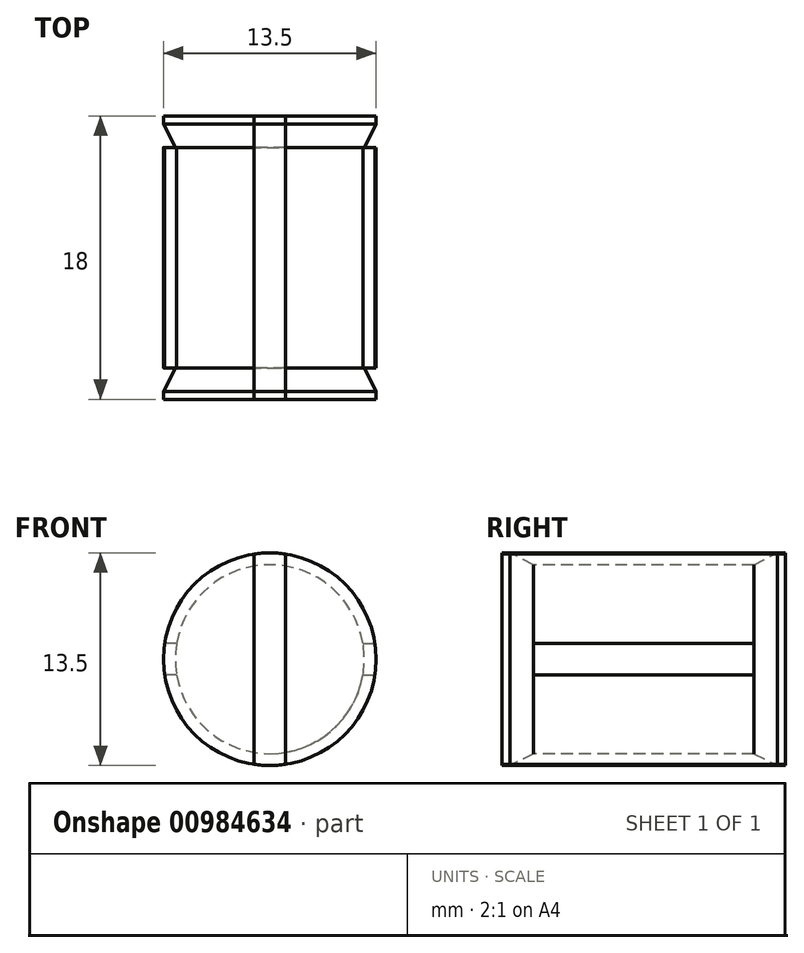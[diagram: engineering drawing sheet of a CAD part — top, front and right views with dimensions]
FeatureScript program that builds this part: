
annotation { "Feature Type Name" : "Feature", "Feature Type Description" : "" }
export const myFeature = defineFeature(function(context is Context, id is Id, definition is map)
    precondition{}
    {
        {
            var Q0;
            Q0=qCreatedBy(makeId("Top.planeOp"),FACE);
            var sketch = newSketch(context, id + "F0", { "sketchPlane" : qUnion([Q0])});
            skLineSegment(sketch, "E0", {"start": v(0, 0) * mm, "end": v(0, 11.4) * mm, "construction": true});
            skLineSegment(sketch, "E1.bottom", {"start": v(0, 19.36) * mm, "end": v(-6, 19.36) * mm});
            skLineSegment(sketch, "E1.top", {"start": v(0, 1.36) * mm, "end": v(-6, 1.36) * mm});
            skLineSegment(sketch, "E1.left", {"start": v(0, 19.36) * mm, "end": v(0, 1.36) * mm});
            skLineSegment(sketch, "E1.right", {"start": v(-6, 19.36) * mm, "end": v(-6, 1.36) * mm});
            skLineSegment(sketch, "E2.bottom", {"start": v(-6, 17.36) * mm, "end": v(-21, 17.36) * mm});
            skLineSegment(sketch, "E2.top", {"start": v(-6, 3.36) * mm, "end": v(-21, 3.36) * mm});
            skLineSegment(sketch, "E2.left", {"start": v(-6, 17.36) * mm, "end": v(-6, 3.36) * mm});
            skLineSegment(sketch, "E2.right", {"start": v(-21, 17.36) * mm, "end": v(-21, 3.36) * mm});
            skLineSegment(sketch, "E3", {"start": v(-3.75, 17.36) * mm, "end": v(-3.75, 19.36) * mm, "construction": true});
            skLineSegment(sketch, "E4", {"start": v(-3.85, 3.36) * mm, "end": v(-3.85, 1.36) * mm, "construction": true});
            skLineSegment(sketch, "E5", {"start": v(-15, 17.36) * mm, "end": v(-15, 3.36) * mm});
            skPoint(sketch, "E6", {"position": v(-18, 10.36) * mm});
            skPoint(sketch, "E6.positionSnap0", {"position": v(-21, 10.36) * mm});
            skLineSegment(sketch, "E7", {"start": v(-18, 10.36) * mm, "end": v(-21, 10.36) * mm, "construction": true});
            skCircle(sketch, "E8", {"center": v(-18, 10.36) * mm, "radius": 1.6 * mm});
            skLineSegment(sketch, "E9", {"start": v(-6.75, 19.36) * mm, "end": v(-6, 19.36) * mm});
            skLineSegment(sketch, "E10", {"start": v(-6.75, 19.36) * mm, "end": v(-6.75, 18.86) * mm});
            skLineSegment(sketch, "E11", {"start": v(-6.75, 18.86) * mm, "end": v(-6, 17.36) * mm});
            skLineSegment(sketch, "E12", {"start": v(0, 10.36) * mm, "end": v(-8.05, 10.36) * mm, "construction": true});
            skLineSegment(sketch, "E13.MirrorCS", {"start": v(-6.75, 1.86) * mm, "end": v(-6, 3.36) * mm});
            skLineSegment(sketch, "E14.MirrorCS", {"start": v(-6.75, 1.36) * mm, "end": v(-6, 1.36) * mm});
            skLineSegment(sketch, "E15.MirrorCS", {"start": v(-6.75, 1.36) * mm, "end": v(-6.75, 1.86) * mm});
            skSolve(sketch);
        }
        {
            var Q0;
            {var subQ4=sQuery(id+"F0.wireOp",EDGE,"E1.bottom");Q0=makeQuery(id+"F0.imprint","IMPRINT",FACE,{"disambiguationData":[TD([[makeQuery(id+"F0.imprint","IMPRINT",EDGE,{"derivedFrom":subQ4}),1.0]])]});}
            var Q1;
            {var subQ2=sQuery(id+"F0.wireOp",EDGE,"q140t8Uf-aWBw-vlao-tcG7-tUnPmBu3D4Ii");Q1=makeQuery(id+"F0.imprint","IMPRINT",FACE,{"disambiguationData":[TD([[makeQuery(id+"F0.imprint","IMPRINT",EDGE,{"derivedFrom":subQ2}),-1.0]])]});}
            var Q2;
            {var subQ0=sQuery(id+"F0.wireOp",EDGE,"E9");Q2=makeQuery(id+"F0.imprint","IMPRINT",FACE,{"disambiguationData":[TD([[makeQuery(id+"F0.imprint","IMPRINT",EDGE,{"derivedFrom":subQ0}),-1.0]])]});}
            var Q3;
            {var subQ2=sQuery(id+"F0.wireOp",EDGE,"E13.MirrorCS");Q3=makeQuery(id+"F0.imprint","IMPRINT",FACE,{"disambiguationData":[TD([[makeQuery(id+"F0.imprint","IMPRINT",EDGE,{"derivedFrom":subQ2}),-1.0]])]});}
            var Q4;
            Q4=sQuery(id+"F0.wireOp",EDGE,"E0");
            revolve(context, id + "F1", {"surfaceOperationType" : NewSurfaceOperationType.NEW, "entities" : qUnion([Q0, Q1, Q2, Q3]), "axis" : qUnion([Q4]), "revolveType" : RevolveType.FULL});
        }
        {
            var Q0;
            Q0=sQuery(id+"F0.wireOp",EDGE,"E2.top");
            cPlane(context, id + "F2", {"entities" : qUnion([Q0]), "cplaneType" : CPlaneType.LINE_ANGLE, "offset" : 25 * mm, "angle" : 0 * degree, "width" : 150 * mm, "height" : 150 * mm});
        }
        {
            var Q0;
            Q0=qCreatedBy(id+"F2.planeOp",FACE);
            var sketch = newSketch(context, id + "F3", { "sketchPlane" : qUnion([Q0])});
            skLineSegment(sketch, "E16.0", {"start": v(-6, 0) * mm, "end": v(-21, 0) * mm});
            skLineSegment(sketch, "E17", {"start": v(-5.92, 1) * mm, "end": v(-21, 1) * mm});
            skLineSegment(sketch, "E18", {"start": v(-21, 1) * mm, "end": v(-21, 0) * mm});
            skLineSegment(sketch, "E19", {"start": v(-5.92, -1) * mm, "end": v(-21, -1) * mm});
            skLineSegment(sketch, "E20", {"start": v(-21, -1) * mm, "end": v(-21, 0) * mm});
            skLineSegment(sketch, "E21", {"start": v(-7.63, -1) * mm, "end": v(-7.63, 0) * mm, "construction": true});
            skLineSegment(sketch, "E22", {"start": v(-8.72, 0) * mm, "end": v(-8.72, 1) * mm, "construction": true});
            skCircle(sketch, "E23.0", {"center": v(0, 0) * mm, "radius": 6 * mm});
            skSolve(sketch);
        }
        {
            var Q0;
            {var subQ0=sQuery(id+"F3.wireOp",EDGE,"E16.0");Q0=makeQuery(id+"F3.imprint","IMPRINT",FACE,{"disambiguationData":[TD([[makeQuery(id+"F3.imprint","IMPRINT",EDGE,{"derivedFrom":subQ0}),-1.0]])]});}
            var Q1;
            {var subQ0=sQuery(id+"F3.wireOp",EDGE,"E16.0");Q1=makeQuery(id+"F3.imprint","IMPRINT",FACE,{"disambiguationData":[TD([[makeQuery(id+"F3.imprint","IMPRINT",EDGE,{"derivedFrom":subQ0}),1.0]])]});}
            var Q2;
            Q2=sQuery(id+"F0.wireOp",VERTEX,"E2.bottom.end");
            extrude(context, id + "F4", {"entities" : qUnion([Q0, Q1]), "endBound" : BoundingType.UP_TO_VERTEX, "oppositeDirection" : true, "depth" : 25 * mm, "endBoundEntityVertex" : qUnion([Q2]), "offsetDistance" : 25 * mm});
        }
        {
            var Q0;
            Q0=makeQuery(id+"F0.imprint","IMPRINT",FACE,{"disambiguationData":[TD([[makeQuery(id+"F0.imprint","IMPRINT",EDGE,{"derivedFrom":sQuery(id+"F0.wireOp",EDGE,"E8")}),1.0]])]});
            extrude(context, id + "F5", {"entities" : qUnion([Q0]), "operationType" : NewBodyOperationType.REMOVE, "endBound" : BoundingType.SYMMETRIC, "oppositeDirection" : true, "depth" : 25 * mm, "offsetDistance" : 25 * mm});
        }
        {
            var Q0;
            Q0=makeQuery(id+"F4.opExtrude","SWEPT_BODY",BODY,{"disambiguationData":[OSD([sQuery(id+"F3.wireOp",EDGE,"E17"),sQuery(id+"F3.wireOp",EDGE,"E18"),sQuery(id+"F3.wireOp",EDGE,"E19"),sQuery(id+"F3.wireOp",EDGE,"E20"),sQuery(id+"F3.wireOp",EDGE,"E23.0")])]});
            var Q1;
            Q1=qCreatedBy(makeId("Right.planeOp"),FACE);
            mirror(context, id + "F6", {"operationType" : NewBodyOperationType.ADD, "entities" : qUnion([Q0]), "mirrorPlane" : qUnion([Q1])});
        }
        {
            var Q0;
            Q0=qCreatedBy(makeId("Top.planeOp"),FACE);
            var sketch = newSketch(context, id + "F7", { "sketchPlane" : qUnion([Q0])});
            skLineSegment(sketch, "E24.0", {"start": v(6.75, 19.36) * mm, "end": v(-6.75, 19.36) * mm});
            skLineSegment(sketch, "E25.0", {"start": v(6.75, 1.36) * mm, "end": v(-6.75, 1.36) * mm});
            skLineSegment(sketch, "E26.bottom", {"start": v(-1, 19.36) * mm, "end": v(1, 19.36) * mm});
            skLineSegment(sketch, "E26.top", {"start": v(-1, 1.36) * mm, "end": v(1, 1.36) * mm});
            skLineSegment(sketch, "E26.left", {"start": v(-1, 19.36) * mm, "end": v(-1, 1.36) * mm});
            skLineSegment(sketch, "E26.right", {"start": v(1, 19.36) * mm, "end": v(1, 1.36) * mm});
            skPoint(sketch, "E27", {"position": v(0, 19.36) * mm});
            skLineSegment(sketch, "E28.0", {"start": v(0, 19.36) * mm, "end": v(0, 1.36) * mm});
            skSolve(sketch);
        }
        {
            var Q0;
            Q0 = qSketchRegion(id + "F7", true);
            extrude(context, id + "F8", {"entities" : qUnion([Q0]), "endBound" : BoundingType.SYMMETRIC, "depth" : 25 * mm, "offsetDistance" : 25 * mm});
        }
        {
            var Q0;
            Q0=makeQuery(id+"F1.opRevolve","SWEPT_FACE",FACE,{"disambiguationData":[OSD([sQuery(id+"F0.wireOp",EDGE,"E1.top"),sQuery(id+"F0.wireOp",EDGE,"E14.MirrorCS")])]});
            var sketch = newSketch(context, id + "F9", { "sketchPlane" : qUnion([Q0])});
            skCircle(sketch, "E29.0", {"center": v(0, 0) * mm, "radius": 6.75 * mm});
            skSolve(sketch);
        }
        {
            var Q0;
            Q0 = qSketchRegion(id + "F9", true);
            var Q1;
            Q1=makeQuery(id+"F1.opRevolve","SWEPT_FACE",FACE,{"disambiguationData":[OSD([sQuery(id+"F0.wireOp",EDGE,"E1.bottom"),sQuery(id+"F0.wireOp",EDGE,"E9")])]});
            extrude(context, id + "F10", {"entities" : qUnion([Q0]), "operationType" : NewBodyOperationType.INTERSECT, "endBound" : BoundingType.UP_TO_SURFACE, "oppositeDirection" : true, "depth" : 25 * mm, "endBoundEntityFace" : qUnion([Q1]), "offsetDistance" : 25 * mm});
        }
    });
